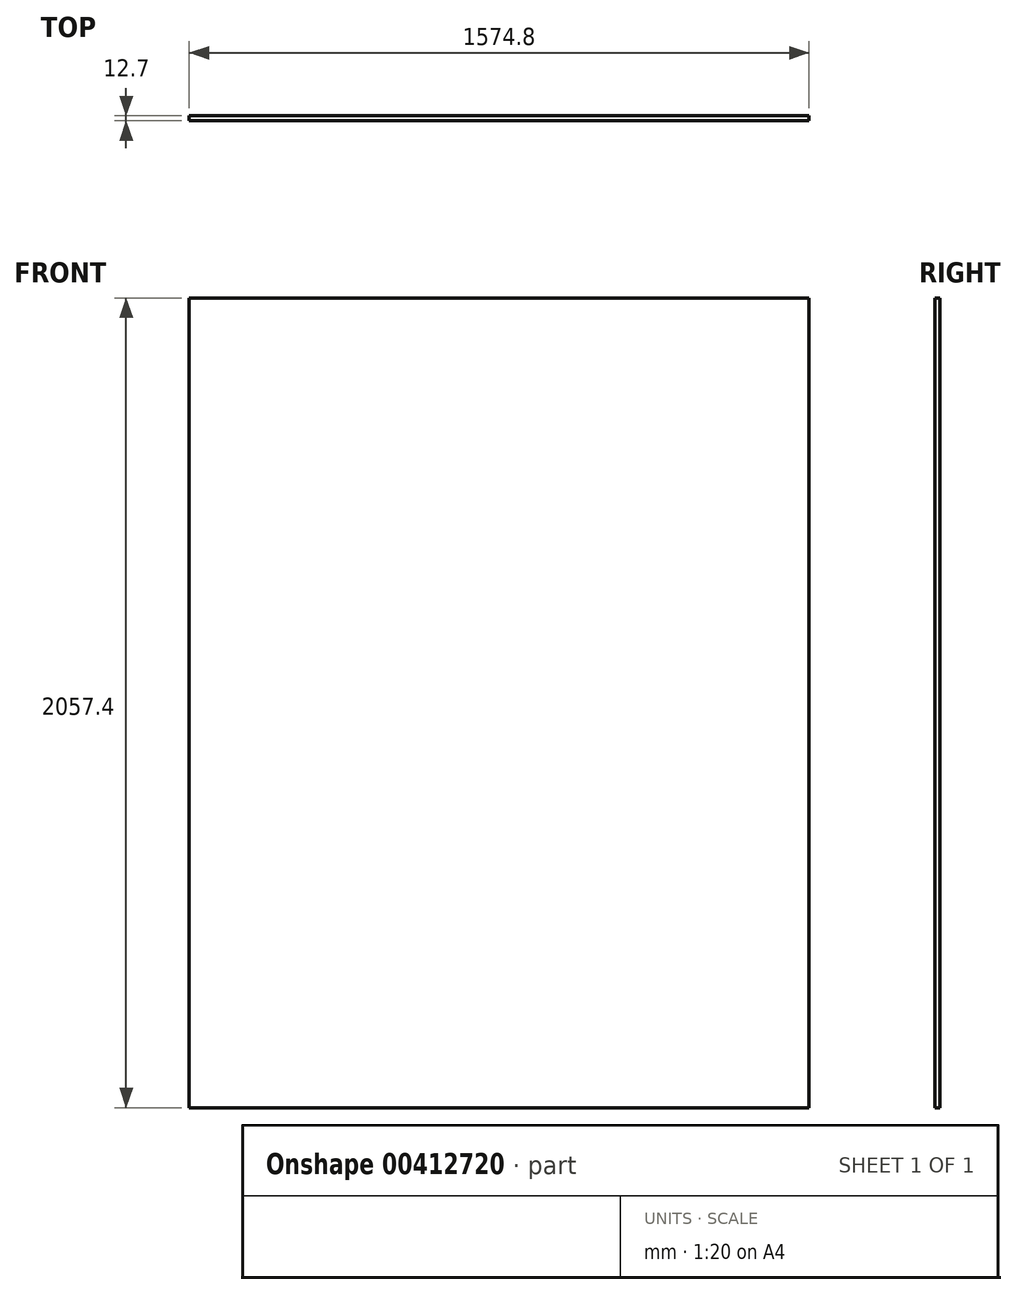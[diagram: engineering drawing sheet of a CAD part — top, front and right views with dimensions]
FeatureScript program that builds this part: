
annotation { "Feature Type Name" : "Feature", "Feature Type Description" : "" }
export const myFeature = defineFeature(function(context is Context, id is Id, definition is map)
    precondition{}
    {
        {
            var Q0;
            Q0=qCreatedBy(makeId("Front.planeOp"),FACE);
            var sketch = newSketch(context, id + "F0", { "sketchPlane" : qUnion([Q0])});
            skLineSegment(sketch, "E0.bottom", {"start": v(-789.05, 1317.84) * mm, "end": v(785.75, 1317.84) * mm});
            skLineSegment(sketch, "E0.top", {"start": v(-789.05, -739.56) * mm, "end": v(785.75, -739.56) * mm});
            skLineSegment(sketch, "E0.left", {"start": v(-789.05, 1317.84) * mm, "end": v(-789.05, -739.56) * mm});
            skLineSegment(sketch, "E0.right", {"start": v(785.75, 1317.84) * mm, "end": v(785.75, -739.56) * mm});
            skSolve(sketch);
        }
        {
            var Q0;
            Q0=makeQuery(id+"F0.imprint","IMPRINT",FACE,{"disambiguationData":[TD([[makeQuery(id+"F0.imprint","IMPRINT",EDGE,{"derivedFrom":sQuery(id+"F0.wireOp",EDGE,"E0.bottom")}),-1.0]])]});
            extrude(context, id + "F1", {"entities" : qUnion([Q0]), "depth" : 12.7 * mm});
        }
    });
